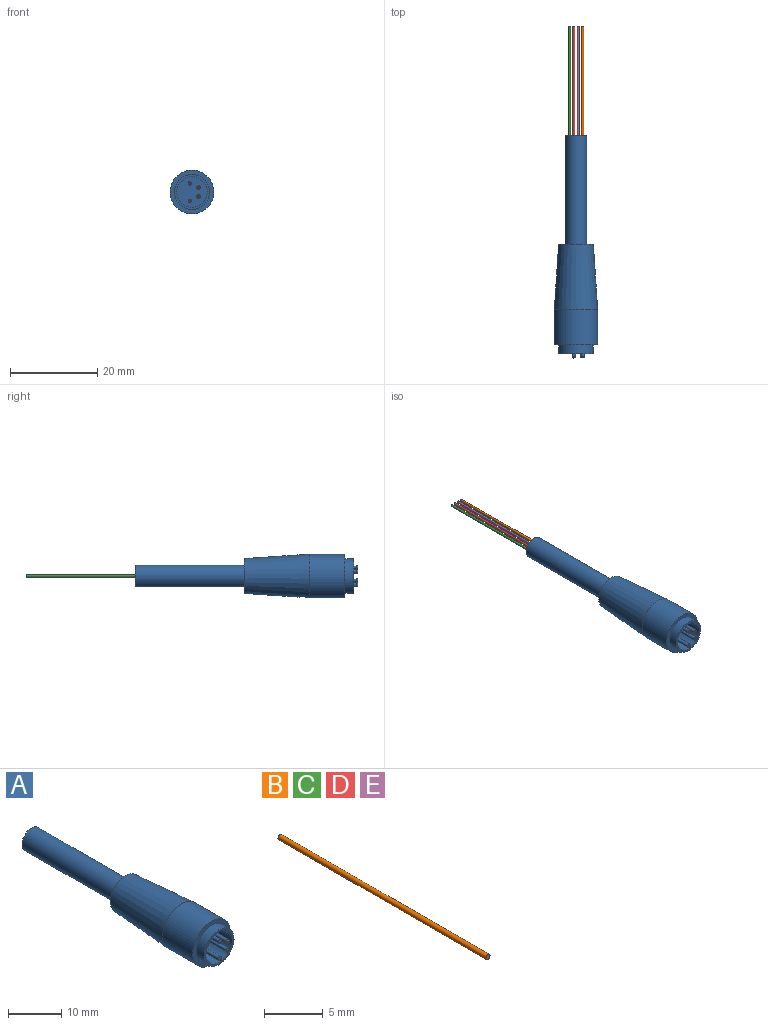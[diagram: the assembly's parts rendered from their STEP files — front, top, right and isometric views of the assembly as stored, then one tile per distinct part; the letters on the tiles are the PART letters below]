
ASSEMBLY  parts=5 mates=4
PART A: 22 faces, bbox 10x51x10 mm
  f0: plane 8x8mm, normal (0,-1,0), area 11.8mm2, adj f5,f6
  f1: plane 8x8mm, normal (0,1,0), area 30.6mm2, adj f2,f20
  f2: cone r=5mm half-angle=3.8deg, axis (0,-1,0), area 425.1mm2, adj f1,f3
  f3: cylinder r=5mm len=10mm, axis (0,1,0), area 251.3mm2, adj f2,f4
  f4: plane 10x10mm, normal (0,-1,0), area 28.3mm2, adj f3,f5
  f5: cylinder r=4mm len=8mm, axis (0,1,0), area 50.3mm2, adj f0,f4
  f6: cylinder r=3.5mm len=8mm, axis (0,-1,0), area 175.9mm2, adj f0,f7
  f7: plane 7x7mm, normal (0,-1,0), area 36.5mm2, adj f6,f8,f10,f12,f14
  f8: cylinder r=0.4mm len=8.75mm, axis (0,1,0), area 22mm2, adj f7,f19
  f9: plane 0.3x0.3mm, normal (0,-1,0), area 0.1mm2, adj f19
  f10: cylinder r=0.4mm len=8.75mm, axis (0,1,0), area 22mm2, adj f7,f18
  f11: plane 0.3x0.3mm, normal (0,-1,0), area 0.1mm2, adj f18
  f12: cylinder r=0.4mm len=8.75mm, axis (0,1,0), area 22mm2, adj f7,f17
  f13: plane 0.3x0.3mm, normal (0,-1,0), area 0.1mm2, adj f17
  f14: cylinder r=0.4mm len=8.75mm, axis (0,1,0), area 22mm2, adj f7,f16
  f15: plane 0.3x0.3mm, normal (0,-1,0), area 0.1mm2, adj f16
  f16: torus R=0.15mm, axis (0,-1,0), area 0.8mm2, adj f14,f15
  f17: torus R=0.15mm, axis (0,-1,0), area 0.8mm2, adj f12,f13
  f18: torus R=0.15mm, axis (0,-1,0), area 0.8mm2, adj f10,f11
  f19: torus R=0.15mm, axis (0,-1,0), area 0.8mm2, adj f8,f9
  f20: cylinder r=2.5mm len=25mm, axis (0,-1,0), area 392.7mm2, adj f1,f21
  f21: plane 5x5mm, normal (0,1,0), area 19.6mm2, adj f20
PART B: 3 faces, bbox 0.5x25x0.5 mm
  f0: cylinder r=0.25mm len=25mm, axis (0,1,0), area 39.3mm2, adj f1,f2
  f1: plane 0.5x0.5mm, normal (0,-1,0), area 0.2mm2, adj f0
  f2: plane 0.5x0.5mm, normal (0,1,0), area 0.2mm2, adj f0
PART C: same geometry as B
PART D: same geometry as B
PART E: same geometry as B
PLACE A t=(-5.07,-21.92,8.26)mm fixed
PLACE B rot(axis=(1,0,0),180deg) t=(-3.57,40.58,8.26)mm
PLACE C t=(-6.57,40.58,8.26)mm
PLACE D rot(axis=(1,0,0),180deg) t=(-5.57,40.58,8.26)mm
PLACE E rot(axis=(1,0,0),180deg) t=(-4.57,40.58,8.26)mm
MATE fastened C.f0 <-> A.f21  axis (0,-1,0) through (-6.57,28.08,8.26)mm
MATE fastened B.f0 <-> A.f21  axis (0,-1,0) through (-3.57,28.08,8.26)mm
MATE fastened D.f0 <-> A.f21  axis (0,-1,0) through (-5.57,28.08,8.26)mm
MATE fastened E.f0 <-> A.f21  axis (0,-1,0) through (-4.57,28.08,8.26)mm
